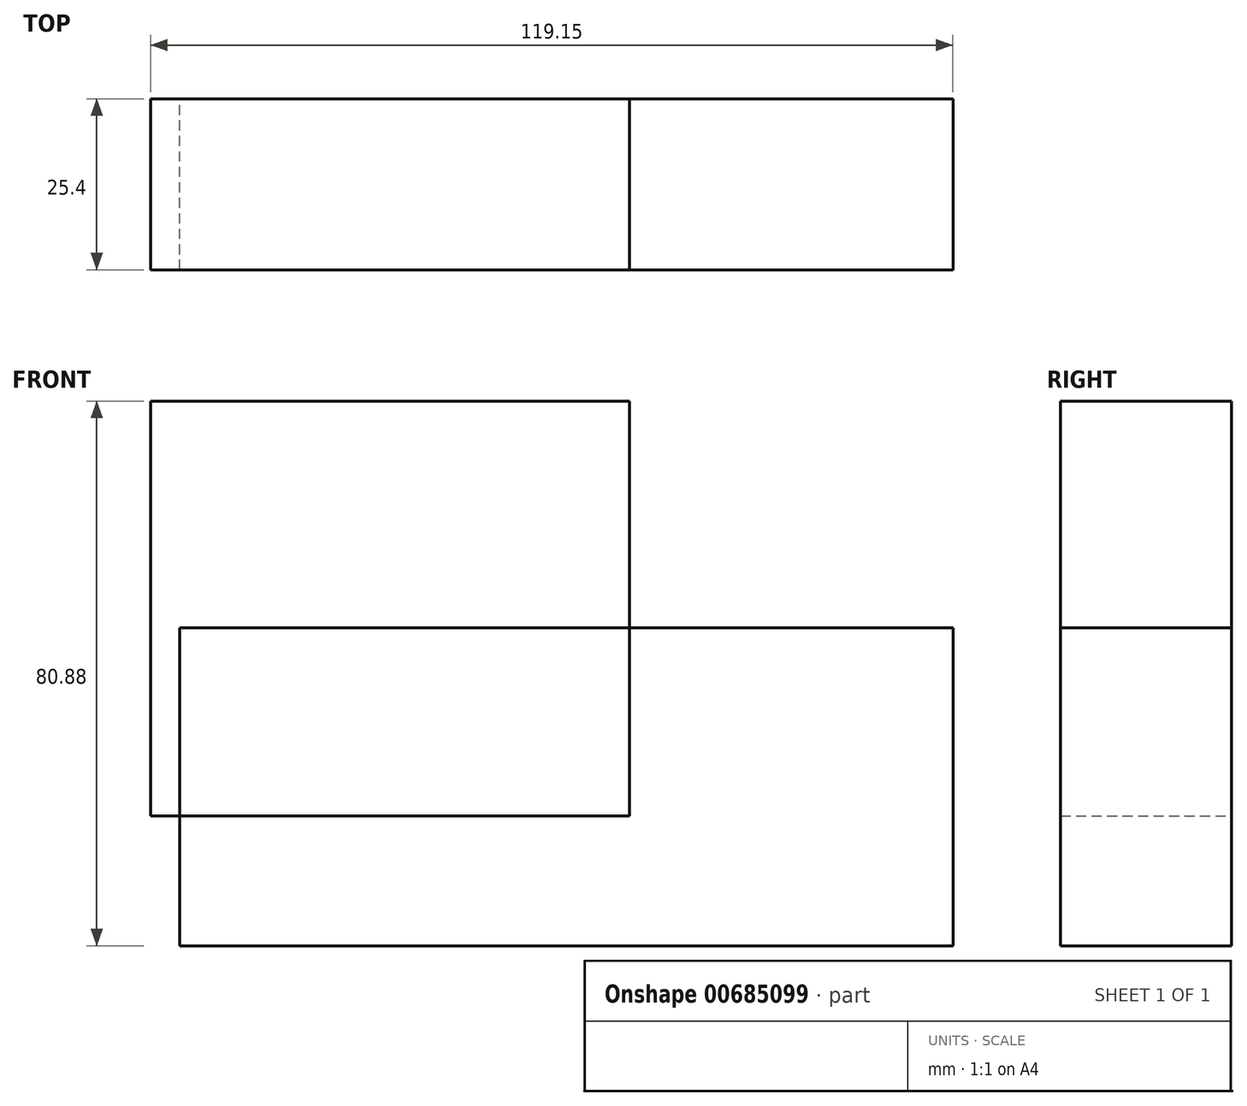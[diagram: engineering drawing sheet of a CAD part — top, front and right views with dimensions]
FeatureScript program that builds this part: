
annotation { "Feature Type Name" : "Feature", "Feature Type Description" : "" }
export const myFeature = defineFeature(function(context is Context, id is Id, definition is map)
    precondition{}
    {
        {
            var Q0;
            Q0=qCreatedBy(makeId("Front.planeOp"),FACE);
            var sketch = newSketch(context, id + "F0", { "sketchPlane" : qUnion([Q0])});
            skLineSegment(sketch, "E0.bottom", {"start": v(-49.07, -39) * mm, "end": v(65.76, -39) * mm});
            skLineSegment(sketch, "E0.top", {"start": v(-49.07, 8.2) * mm, "end": v(65.76, 8.2) * mm});
            skLineSegment(sketch, "E0.left", {"start": v(-49.07, -39) * mm, "end": v(-49.07, 8.2) * mm});
            skLineSegment(sketch, "E0.right", {"start": v(65.76, -39) * mm, "end": v(65.76, 8.2) * mm});
            skLineSegment(sketch, "E1.bottom", {"start": v(17.7, -19.71) * mm, "end": v(-53.39, -19.71) * mm});
            skLineSegment(sketch, "E1.top", {"start": v(17.7, 41.88) * mm, "end": v(-53.39, 41.88) * mm});
            skLineSegment(sketch, "E1.left", {"start": v(17.7, -19.71) * mm, "end": v(17.7, 41.88) * mm});
            skLineSegment(sketch, "E1.right", {"start": v(-53.39, -19.71) * mm, "end": v(-53.39, 41.88) * mm});
            skSolve(sketch);
        }
        {
            var Q0;
            {var subQ0=sQuery(id+"F0.wireOp",EDGE,"E1.top");Q0=makeQuery(id+"F0.imprint","IMPRINT",FACE,{"disambiguationData":[TD([[makeQuery(id+"F0.imprint","IMPRINT",EDGE,{"derivedFrom":subQ0}),1.0]])]});}
            var Q1;
            {var subQ1=sQuery(id+"F0.wireOp",EDGE,"E0.bottom");Q1=makeQuery(id+"F0.imprint","IMPRINT",FACE,{"disambiguationData":[TD([[makeQuery(id+"F0.imprint","IMPRINT",EDGE,{"derivedFrom":subQ1}),1.0]])]});}
            extrude(context, id + "F1", {"entities" : qUnion([Q0, Q1]), "depth" : 25.4 * mm, "offsetDistance" : 25.4 * mm});
        }
    });
